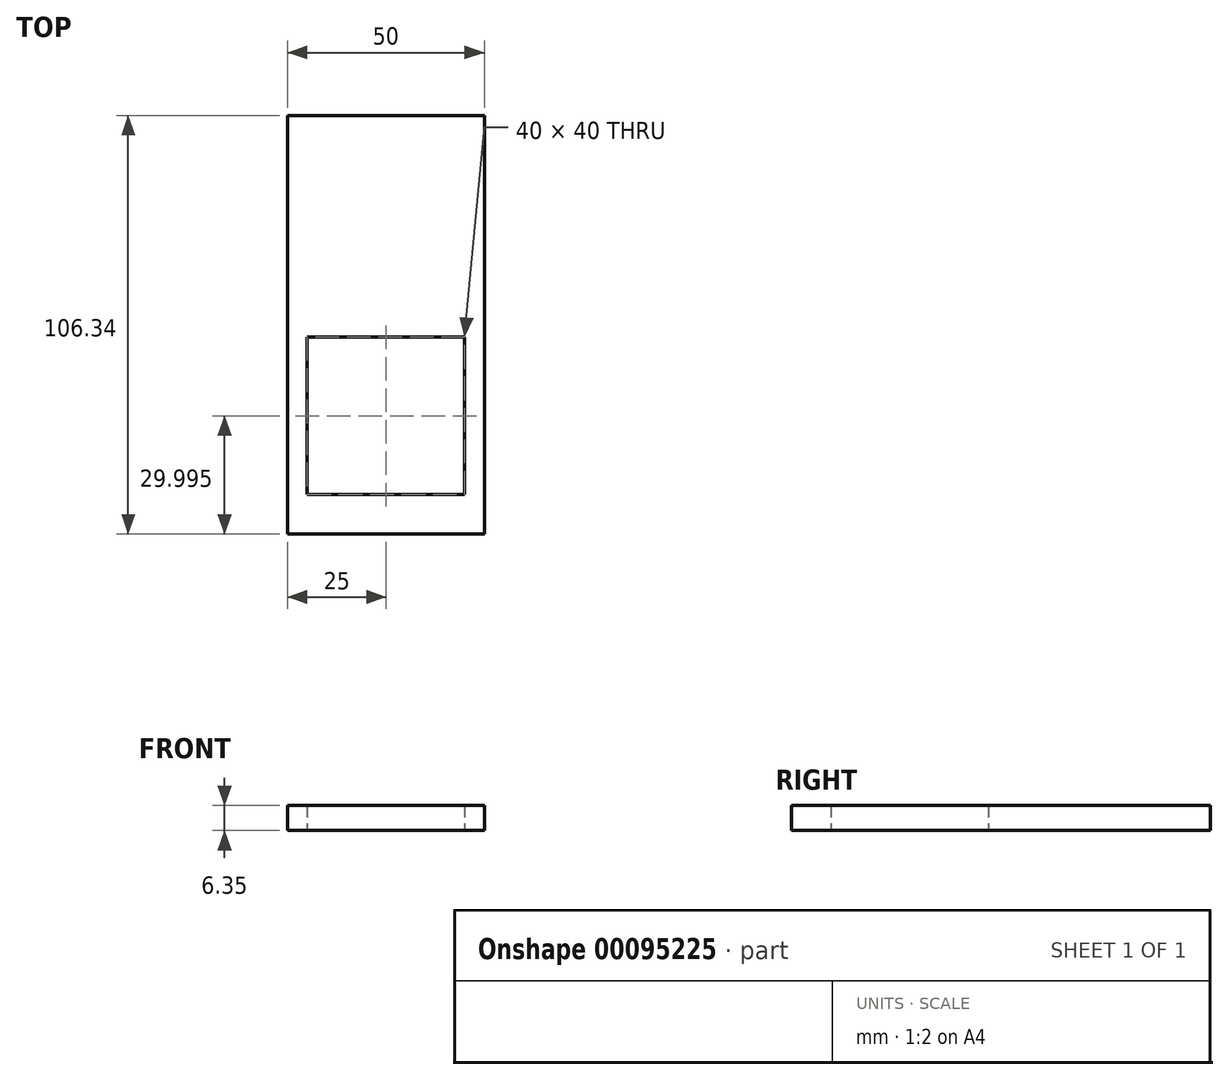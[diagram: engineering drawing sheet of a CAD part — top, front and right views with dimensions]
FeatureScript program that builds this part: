
annotation { "Feature Type Name" : "Feature", "Feature Type Description" : "" }
export const myFeature = defineFeature(function(context is Context, id is Id, definition is map)
    precondition{}
    {
        {
            var Q0;
            Q0=qCreatedBy(makeId("Top.planeOp"),FACE);
            var sketch = newSketch(context, id + "F0", { "sketchPlane" : qUnion([Q0])});
            skLineSegment(sketch, "E0.bottom", {"start": v(25, 53.17) * mm, "end": v(-25, 53.17) * mm});
            skLineSegment(sketch, "E0.top", {"start": v(25, -53.17) * mm, "end": v(-25, -53.17) * mm});
            skLineSegment(sketch, "E0.left", {"start": v(25, 53.17) * mm, "end": v(25, -53.17) * mm});
            skLineSegment(sketch, "E0.right", {"start": v(-25, 53.17) * mm, "end": v(-25, -53.17) * mm});
            skPoint(sketch, "E0.middle", {"position": v(0, 0) * mm});
            skLineSegment(sketch, "E1.bottom", {"start": v(20, -43.17) * mm, "end": v(-20, -43.17) * mm});
            skLineSegment(sketch, "E1.top", {"start": v(20, -3.17) * mm, "end": v(-20, -3.18) * mm});
            skLineSegment(sketch, "E1.left", {"start": v(20, -43.17) * mm, "end": v(20, -3.17) * mm});
            skLineSegment(sketch, "E1.right", {"start": v(-20, -43.17) * mm, "end": v(-20, -3.18) * mm});
            skPoint(sketch, "E1.middle", {"position": v(0, -23.18) * mm});
            skLineSegment(sketch, "E2", {"start": v(0, -43.17) * mm, "end": v(0, -53.17) * mm});
            skSolve(sketch);
        }
        {
            var Q0;
            Q0=makeQuery(id+"F0.imprint","IMPRINT",FACE,{"disambiguationData":[TD([[makeQuery(id+"F0.imprint","IMPRINT",EDGE,{"derivedFrom":sQuery(id+"F0.wireOp",EDGE,"E0.bottom")}),1.0]])]});
            extrude(context, id + "F1", {"entities" : qUnion([Q0]), "depth" : 6.35 * mm});
        }
    });
